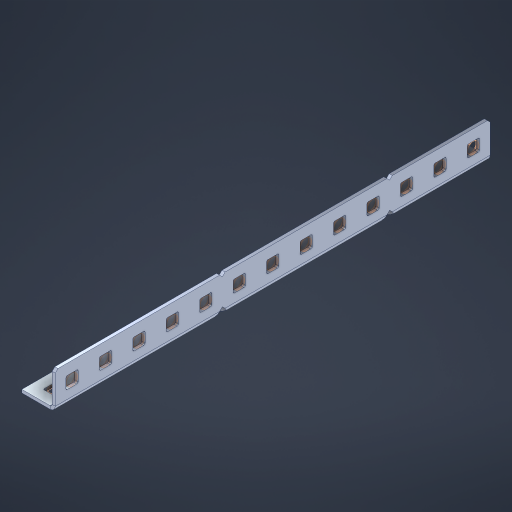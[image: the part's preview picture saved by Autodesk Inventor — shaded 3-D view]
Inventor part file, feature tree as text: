
AUTODESK INVENTOR PART (.ipt)
format: ipt  version: 2023 (Build 270158000, 158)  size: 611,840 bytes
history: native  units: in
note: dims shown in document units (in); Inventor stores cm internally (conversion verified against a paired STEP export)
features: other x31, extrude x25, sheet_metal_op x10, sketch x8, mirror x1, pattern_linear x1, chamfer x1
ambient origin geometry x8: Origin, YZ Plane, XZ Plane, XY Plane, X Axis, Y Axis, Z Axis, Center Point
bodies: Solid1 (feature_tree), Body (feature_tree)
feature tree (77):
  other  "Flange Pattern Plane"
  sheet_metal_op  "Flange Pattern"
  sheet_metal_op  "Body Pattern"
  other  "Arc Length"
  mirror  "Notch Mirror"
  pattern_linear  "Notch Pattern"  Spacing1=0.1875in  [1 undecoded]
  chamfer  "End Chamfer"
  extrude  "Half Cut"  Depth=0.0469in
  sketch  "Sketch1"  dims[d0=2.5in]
  other  "Plate1"
  sketch  "Sketch2"  dims[d1=6.5in]
  other  "Plate2"
  sheet_metal_op  "Bend1"
  sheet_metal_op  "Corner1"
  sketch  "Sketch3"  dims[d2=0.0469in]
  other  "Flange Pattern Sketch"
  sketch  "Sketch7"  dims[d3=0.0469in]
  other  "Srf1"
  other  "Srf2"
  sketch  "Sketch8"  dims[d4=0.0234in]
  sketch  "Sketch9"  dims[d5=0.0938in]
  other  "Srf91"
  sheet_metal_op  "Body Pattern Sketch"
  other  "Srf92"
  sketch  "Sketch13"  dims[d6=0.0469in]
  sketch  "Sketch14"  dims[d7=0.5in d8=90.0deg d9=0.0312in d10=0.1875in d11=0.0469in d12=0.0469in d16=0.182in d17=0.02in d18=0.0469in d19=0.0in d20=0.25in d21=0.25in d46=0.172in d47=1.0in d48=0.0in d49=0.182in d50=0.02in d51=0.25in d52=0.25in d53=0.0469in d54=0.0in d55=0.172in d56=1.0in d57=0.0in d60=5.1181in d62=0.5in d63=0.3937in d65=0.5in d85=0.1227in d86=0.1659in d88=0.04in d89=0.0469in d90=0.0in d91=0.04in d92=0.0491in d95=2.5in d96=0.04in d97=0.25in d98=45.0deg d101=0.0in d102=2.497in d131=0.5in d132=5.1181in d134=0.5in d139=0.5in]
  other  "Srf856"
  other  "Srf1310"
  other  "Srf1311"
  other  "Srf1312"
  other  "Srf1376"
  other  "Srf1377"
  other  "Srf1728"
  other  "Srf1755"
  other  "Srf1878"
  other  "Srf1879"
  other  "Srf1880"
  other  "Srf1881"
  other  "Srf1882"
  other  "Srf1883"
  other  "Srf1884"
  other  "Srf1942"
  other  "Srf1943"
  other  "Srf1944"
  other  "Srf1945"
  other  "Srf1946"
  other  "Srf1947"
  other  "Srf1948"
  sheet_metal_op  "Flange Stamp"
  sheet_metal_op  "Flange Circle"
  sheet_metal_op  "Body Stamp"
  sheet_metal_op  "Body Circle"
  sheet_metal_op  "Notch"
  extrude  "ExtrusionSrf2"  Depth=0.0469in
  extrude  "ExtrusionSrf92"  Depth=0.5in
  extrude  "ExtrusionSrf856"  Depth=0.02in
  extrude  "ExtrusionSrf1310"  Depth=0.0469in
  extrude  "ExtrusionSrf1311"  TaperAngle=0.0deg  [1 undecoded]
  extrude  "ExtrusionSrf1312"  Depth=0.5in
  extrude  "ExtrusionSrf1376"  Depth=0.5in
  extrude  "ExtrusionSrf1377"  Depth=0.5in
  extrude  "ExtrusionSrf1728"  Depth=0.5in TaperAngle=0.0deg
  extrude  "ExtrusionSrf1755"  Depth=0.5in
  extrude  "ExtrusionSrf1878"  Depth=0.02in
  extrude  "ExtrusionSrf1879"  Depth=0.5in
  extrude  "ExtrusionSrf1880"  Depth=0.5in
  extrude  "ExtrusionSrf1881"  Depth=0.0469in
  extrude  "ExtrusionSrf1882"  TaperAngle=0.0deg  [1 undecoded]
  extrude  "ExtrusionSrf1883"  Depth=0.5in
  extrude  "ExtrusionSrf1884"  Depth=0.5in TaperAngle=0.0deg
  extrude  "ExtrusionSrf1942"  Depth=0.5in
  extrude  "ExtrusionSrf1943"  Depth=0.5in
  extrude  "ExtrusionSrf1944"  Depth=0.5in
  extrude  "ExtrusionSrf1945"  Depth=0.5in
  extrude  "ExtrusionSrf1946"  Depth=0.5in
  extrude  "ExtrusionSrf1947"  Depth=0.0469in
  extrude  "ExtrusionSrf1948"  TaperAngle=0.0deg  [1 undecoded]
note: 4 required parameter values undecoded (feature->parameter linkage not recoverable at this tier; creation-order binding heuristic only, values carry confidence <= 0.55)
